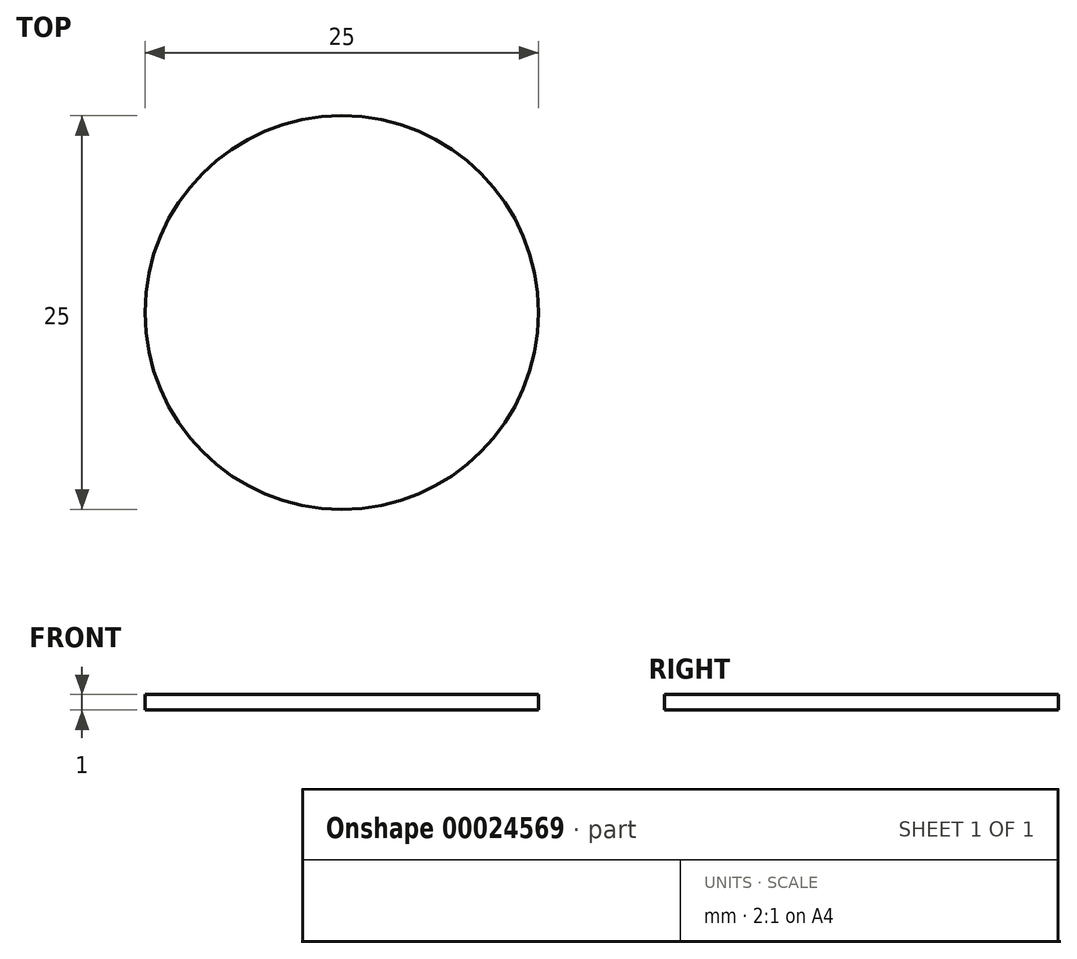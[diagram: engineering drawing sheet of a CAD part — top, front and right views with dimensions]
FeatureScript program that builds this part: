
annotation { "Feature Type Name" : "Feature", "Feature Type Description" : "" }
export const myFeature = defineFeature(function(context is Context, id is Id, definition is map)
    precondition{}
    {
        {
            var Q0;
            Q0=qCreatedBy(makeId("Top.planeOp"),FACE);
            var sketch = newSketch(context, id + "F0", { "sketchPlane" : qUnion([Q0])});
            skCircle(sketch, "E0", {"center": v(0, 0) * mm, "radius": 12.5 * mm});
            skSolve(sketch);
        }
        {
            var Q0;
            Q0=qSketchRegion(id+"F0",true);
            extrude(context, id + "F1", {"entities" : qUnion([Q0]), "endBound" : BoundingType.SYMMETRIC, "depth" : 1 * mm});
        }
    });
